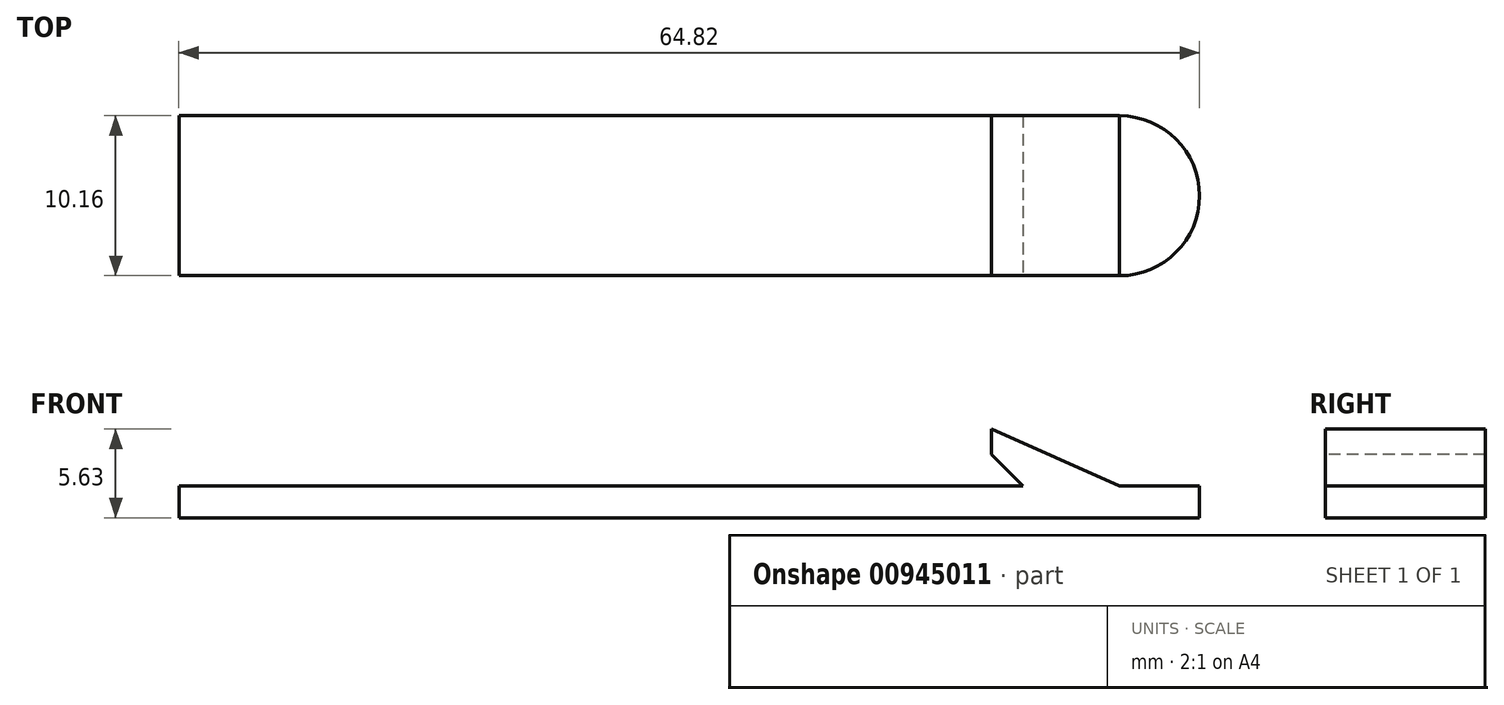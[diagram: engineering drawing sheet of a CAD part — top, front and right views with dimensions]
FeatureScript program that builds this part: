
annotation { "Feature Type Name" : "Feature", "Feature Type Description" : "" }
export const myFeature = defineFeature(function(context is Context, id is Id, definition is map)
    precondition{}
    {
        {
            var Q0;
            Q0=qCreatedBy(makeId("Top.planeOp"),FACE);
            var sketch = newSketch(context, id + "F0", { "sketchPlane" : qUnion([Q0])});
            skLineSegment(sketch, "E0.bottom", {"start": v(-19.76, -30.4) * mm, "end": v(39.98, -30.4) * mm});
            skLineSegment(sketch, "E0.top", {"start": v(-19.76, -40.55) * mm, "end": v(39.98, -40.55) * mm});
            skLineSegment(sketch, "E0.left", {"start": v(-19.76, -30.4) * mm, "end": v(-19.76, -40.55) * mm});
            skLineSegment(sketch, "E0.right", {"start": v(39.98, -30.4) * mm, "end": v(39.98, -40.55) * mm});
            skArc(sketch, "E1", {"start": v(39.98, -40.55) * mm, "mid": v(45.06, -35.47) * mm, "end": v(39.98, -30.4) * mm});
            skSolve(sketch);
        }
        {
            var Q0;
            Q0=qSketchRegion(id+"F0",true);
            extrude(context, id + "F1", {"entities" : qUnion([Q0]), "depth" : 2.03 * mm, "offsetDistance" : 25.4 * mm});
        }
        {
            var Q0;
            Q0=makeQuery(id+"F1.opExtrude","CAP_FACE",FACE,{"disambiguationData":[OSD([sQuery(id+"F0.wireOp",EDGE,"E0.bottom"),sQuery(id+"F0.wireOp",EDGE,"E0.top"),sQuery(id+"F0.wireOp",EDGE,"E0.left"),sQuery(id+"F0.wireOp",EDGE,"E1")])],"isStart":false});
            var sketch = newSketch(context, id + "F2", { "sketchPlane" : qUnion([Q0])});
            skLineSegment(sketch, "E2", {"start": v(-19.76, -32.42) * mm, "end": v(-7.97, -32.42) * mm});
            skLineSegment(sketch, "E3", {"start": v(-19.76, -32.42) * mm, "end": v(-19.76, -30.4) * mm});
            skLineSegment(sketch, "E4", {"start": v(-19.76, -30.4) * mm, "end": v(-19.76, -32.42) * mm});
            skLineSegment(sketch, "E5", {"start": v(-19.76, -34.45) * mm, "end": v(-7.97, -34.45) * mm});
            skLineSegment(sketch, "E6", {"start": v(-19.76, -34.45) * mm, "end": v(-19.76, -32.42) * mm});
            skLineSegment(sketch, "E7", {"start": v(-19.76, -36.49) * mm, "end": v(-7.97, -36.49) * mm});
            skLineSegment(sketch, "E8", {"start": v(-19.76, -36.49) * mm, "end": v(-19.76, -34.45) * mm});
            skLineSegment(sketch, "E9", {"start": v(-19.76, -38.52) * mm, "end": v(-7.97, -38.52) * mm});
            skLineSegment(sketch, "E10", {"start": v(-19.76, -38.52) * mm, "end": v(-19.76, -40.55) * mm});
            skLineSegment(sketch, "E11", {"start": v(-19.76, -40.55) * mm, "end": v(-19.76, -38.52) * mm});
            skLineSegment(sketch, "E12", {"start": v(-7.97, -32.42) * mm, "end": v(-7.97, -34.45) * mm});
            skLineSegment(sketch, "E13", {"start": v(-7.97, -36.49) * mm, "end": v(-7.97, -38.52) * mm});
            skSolve(sketch);
        }
        {
            var Q0;
            Q0=makeQuery(id+"F1.opExtrude","SWEPT_FACE",FACE,{"disambiguationData":[OSD([sQuery(id+"F0.wireOp",EDGE,"E0.top")])]});
            var sketch = newSketch(context, id + "F3", { "sketchPlane" : qUnion([Q0])});
            skLineSegment(sketch, "E14", {"start": v(39.98, 2.03) * mm, "end": v(31.86, 2.03) * mm});
            skLineSegment(sketch, "E15", {"start": v(31.86, 2.03) * mm, "end": v(31.86, 5.63) * mm});
            skLineSegment(sketch, "E16", {"start": v(31.86, 5.63) * mm, "end": v(39.98, 2.03) * mm});
            skSolve(sketch);
        }
        {
            var Q0;
            Q0=qSketchRegion(id+"F3",true);
            extrude(context, id + "F4", {"entities" : qUnion([Q0]), "operationType" : NewBodyOperationType.ADD, "oppositeDirection" : true, "depth" : 10.16 * mm, "offsetDistance" : 25.4 * mm});
        }
        {
            var Q0;
            Q0=makeQuery(id+"F4.boolean.opBoolean","MERGE",FACE,{"derivedFrom":[makeQuery(id+"F1.opExtrude","SWEPT_FACE",FACE,{"disambiguationData":[OSD([sQuery(id+"F0.wireOp",EDGE,"E0.top")])]}),makeQuery(id+"F4.opExtrude","CAP_FACE",FACE,{"disambiguationData":[OSD([sQuery(id+"F3.wireOp",EDGE,"E14"),sQuery(id+"F3.wireOp",EDGE,"E15"),sQuery(id+"F3.wireOp",EDGE,"E16")])],"isStart":true})]});
            var sketch = newSketch(context, id + "F5", { "sketchPlane" : qUnion([Q0])});
            skLineSegment(sketch, "E17", {"start": v(31.86, 4.03) * mm, "end": v(31.86, 2.03) * mm});
            skLineSegment(sketch, "E18", {"start": v(31.86, 2.03) * mm, "end": v(33.86, 2.03) * mm});
            skLineSegment(sketch, "E19", {"start": v(33.86, 2.03) * mm, "end": v(31.86, 4.03) * mm});
            skSolve(sketch);
        }
        {
            var Q0;
            Q0 = qSketchRegion(id + "F5", true);
            extrude(context, id + "F6", {"entities" : qUnion([Q0]), "operationType" : NewBodyOperationType.REMOVE, "endBound" : BoundingType.THROUGH_ALL, "oppositeDirection" : true, "depth" : 25.4 * mm, "offsetDistance" : 25.4 * mm});
        }
    });
